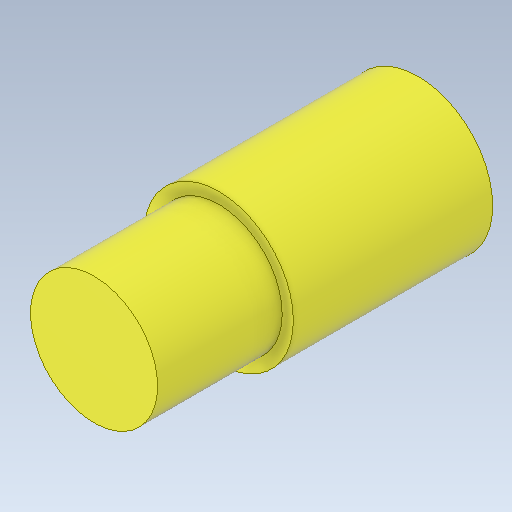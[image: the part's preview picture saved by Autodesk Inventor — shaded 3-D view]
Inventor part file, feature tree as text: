
AUTODESK INVENTOR PART (.ipt)
format: ipt  version: 2020.2 (Build 242310000, 310)  size: 116,224 bytes
history: native  units: mm
features: extrude x2, other x1, sketch x1
ambient origin geometry x8: Origin, YZ Plane, XZ Plane, XY Plane, X Axis, Y Axis, Z Axis, Center Point
bodies: Body1 (feature_tree)
feature tree (4):
  other  "ソリッド1"
  sketch  "スケッチ1"
  extrude  "押し出し1"  Depth=6.0mm
  extrude  "押し出し2"  Depth=5.1mm
